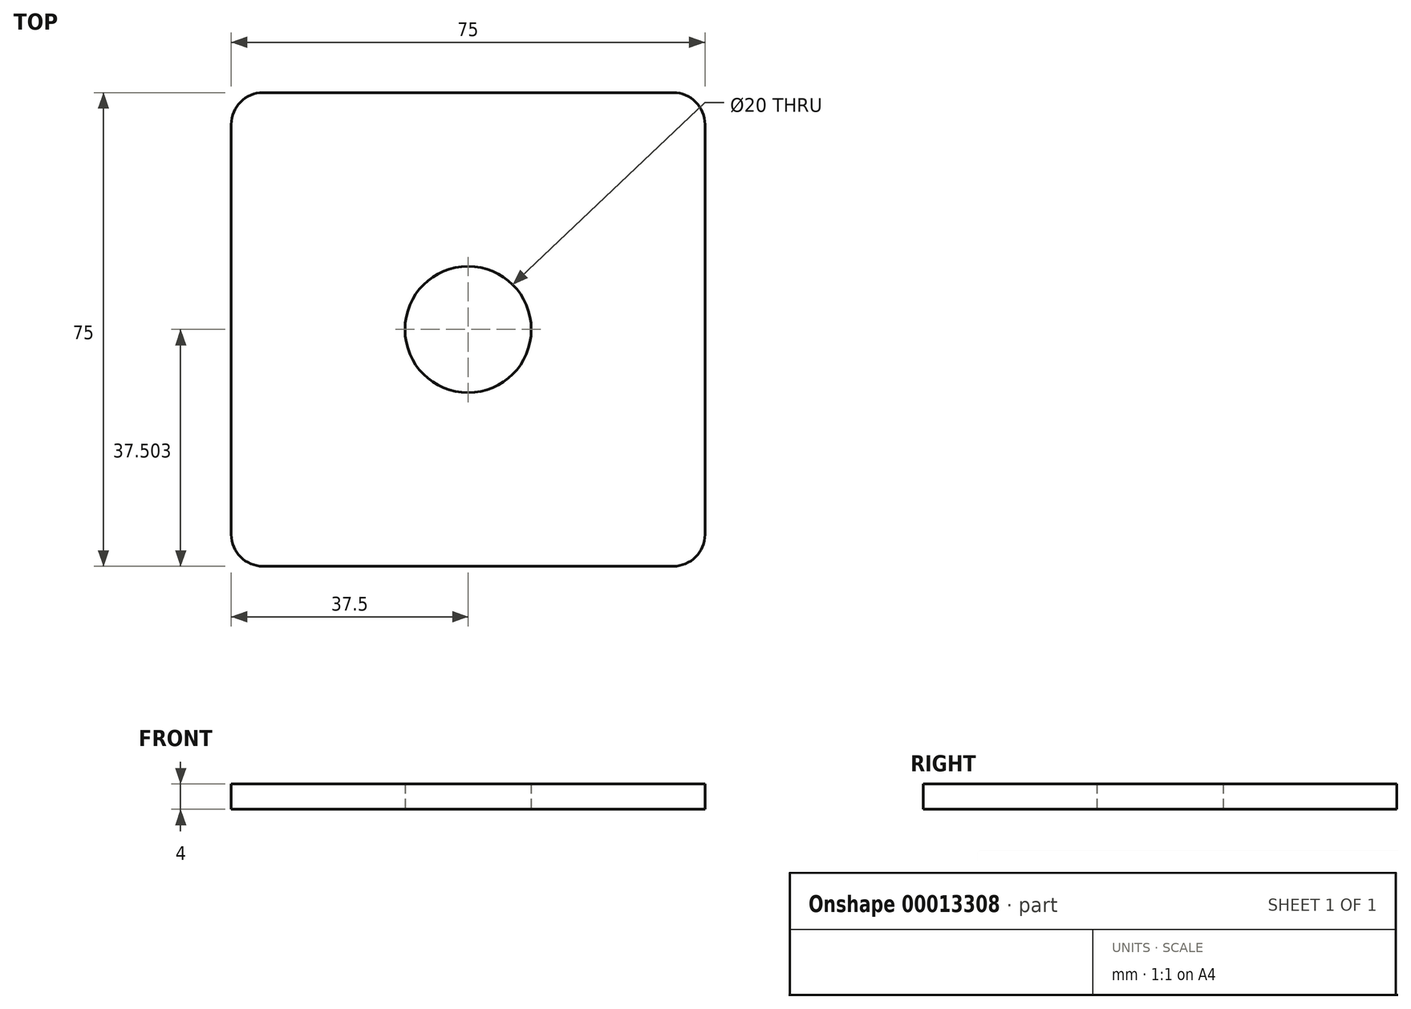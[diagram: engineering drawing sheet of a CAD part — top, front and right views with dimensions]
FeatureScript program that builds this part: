
annotation { "Feature Type Name" : "Feature", "Feature Type Description" : "" }
export const myFeature = defineFeature(function(context is Context, id is Id, definition is map)
    precondition{}
    {
        {
            var Q0;
            Q0=qCreatedBy(makeId("Top.planeOp"),FACE);
            var sketch = newSketch(context, id + "F0", { "sketchPlane" : qUnion([Q0])});
            skLineSegment(sketch, "E0.bottom", {"start": v(-30.44, 40.33) * mm, "end": v(34.56, 40.33) * mm});
            skLineSegment(sketch, "E0.top", {"start": v(-30.44, -34.67) * mm, "end": v(34.56, -34.67) * mm});
            skLineSegment(sketch, "E0.left", {"start": v(-35.44, 35.33) * mm, "end": v(-35.44, -29.67) * mm});
            skLineSegment(sketch, "E0.right", {"start": v(39.56, 35.33) * mm, "end": v(39.56, -29.67) * mm});
            skCircle(sketch, "E1", {"center": v(2.06, 2.83) * mm, "radius": 10 * mm});
            skPoint(sketch, "E2.visualSharp", {"position": v(-35.44, 40.33) * mm});
            skArc(sketch, "E2.filletArc", {"start": v(-30.44, 40.33) * mm, "mid": v(-33.98, 38.87) * mm, "end": v(-35.44, 35.33) * mm});
            skPoint(sketch, "E3.visualSharp", {"position": v(39.56, 40.33) * mm});
            skArc(sketch, "E3.filletArc", {"start": v(39.56, 35.33) * mm, "mid": v(38.1, 38.87) * mm, "end": v(34.56, 40.33) * mm});
            skPoint(sketch, "E4.visualSharp", {"position": v(39.56, -34.67) * mm});
            skArc(sketch, "E4.filletArc", {"start": v(34.56, -34.67) * mm, "mid": v(38.1, -33.2) * mm, "end": v(39.56, -29.67) * mm});
            skPoint(sketch, "E5.visualSharp", {"position": v(-35.44, -34.67) * mm});
            skArc(sketch, "E5.filletArc", {"start": v(-35.44, -29.67) * mm, "mid": v(-33.98, -33.2) * mm, "end": v(-30.44, -34.67) * mm});
            skSolve(sketch);
        }
        {
            var Q0;
            Q0 = qSketchRegion(id + "F0", true);
            extrude(context, id + "F1", {"entities" : qUnion([Q0]), "depth" : 4 * mm});
        }
    });
